# Revit family: PRD_FrankeWS_WstBins_WasteBin_CHRX607,CHRX608
name_source: partatom
category: Furniture
revit_build: Autodesk Revit 2018 (Build: 20190510_1515(x64)
units: mm (PartAtom-declared; Revit-internal decimal feet)

## family parameters
Always vertical = Yes
Cut with Voids When Loaded = No
OmniClass Number = 23.40.20.31.11
OmniClass Title = Bins
Room Calculation Point = No
Shared = No
Work Plane-Based = No

## types (2) — shared parameters
AssetType = Movable
Category = Pr_40_50_07_96, Waste bins
Color = Stainless steel
Description = Waste bin free standing or for wall mounting, stainless steel, surface satin finished, wire thickness 2 mm, square perforated fascia pattern, incl. stainless steel screws and dowels.
DurationUnit = year
Finish = Satin finished
FinishAndColour = Stainless steel, satin finished
Form = Freestanding
IfcExportAs = IfcFurnitureType
IfcExportType = NOTDEFINED
MainColor = Stainless steel
Manufacturer = KWC Group AG
ManufacturerName = KWC Group AG
ManufacturerURL = www.kwc.com
Material = Stainless steel
Materials = Stainless steel 1.4301
NBSDescription = Waste bins
NBSReference = 45-35-72/380
ProductInformation = https://pim.kwc.com
Style = Waste bin
URL = www.kwc.com
Uniclass2015Code = Pr_40_50_07_96
Uniclass2015Title = Waste bins
Uniclass2015Version = Products v1.10
Version = 1
WarrantyDurationUnit = year
WasteBinMaterial = PRD_AR_StainlessSteel_SatinFinished_Wire

## per-type parameters (varying)
| type | BIMObjectName | Features | GrossWeight | ModelNumber | Name | NetWeight | NominalDepth | NominalHeight | NominalWidth | Size |
| CHRX607 | PRD_AR_WasteBins_WasteBin_CHRX607 | stainless steel, 2.00 mm, satin finished, wall mounting, 440x628x315 mm (WxHxD) | 3.10 kg | 2000057137 | Waste bin CHRX607 | 3.10 kg | 315 mm  [stored 1.03346 ft] | 628 mm  [stored 2.06037 ft] | 440 mm  [stored 1.44357 ft] | 440 x 628 x 315 mm |
| CHRX608 | PRD_AR_WasteBins_WasteBin_CHRX608 | stainless steel, 2.00 mm, satin finished, wall mounting, 350x505x252 mm (WxHxD) | 2.00 kg | 2000057138 | Waste bin CHRX608 | 1.70 kg | 252 mm  [stored 0.826772 ft] | 505 mm  [stored 1.65682 ft] | 350 mm  [stored 1.14829 ft] | 350 x 505 x 252 mm |

note: column(s) folded — value = type name in every type: Model, ModelReference, Type

note: [stored X ft] marks values corroborated as IEEE doubles in the binary element streams (Revit-internal decimal feet)

## geometry (parser evidence)
native form markers: Sweep x8
no freeform markers — native parametric forms only
